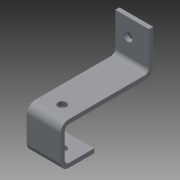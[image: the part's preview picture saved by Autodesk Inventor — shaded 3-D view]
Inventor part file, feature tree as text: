
AUTODESK INVENTOR PART (.ipt)
format: ipt  version: 2013 (Build 170138000, 138)  size: 134,144 bytes
history: native  units: in
note: dims shown in document units (in); Inventor stores cm internally (conversion verified against a paired STEP export)
features: sheet_metal_op x10, sketch x5, other x4, extrude x1, reference x1
ambient origin geometry x8: Origin, YZ Plane, XZ Plane, XY Plane, X Axis, Y Axis, Z Axis, Center Point
bodies: Solid1 (feature_tree)
feature tree (21):
  sheet_metal_op  "Face1"
  sheet_metal_op  "Flange1"
  sheet_metal_op  "Flange2"
  sheet_metal_op  "Flange3"
  extrude  "Extrusion1"  Depth=0.125in
  sketch  "Sketch1"  dims[d0=0.125in d1=0.125in]
  other  "Plate1"
  sketch  "Sketch2"  dims[d2=0.0625in]
  other  "Plate2"
  sheet_metal_op  "Bend1"
  sheet_metal_op  "Corner1"
  sketch  "Sketch3"  dims[d3=0.25in]
  other  "Plate3"
  sheet_metal_op  "Bend2"
  sheet_metal_op  "Corner2"
  sketch  "Sketch4"  dims[d4=0.125in]
  other  "Plate4"
  sheet_metal_op  "Bend3"
  sheet_metal_op  "Corner3"
  sketch  "Sketch5"  dims[d5=2.5in d6=90.0deg d7=0.125in d8=0.5in d9=0.125in d10=0.125in d11=0.125in d12=0.0625in d13=0.25in d14=0.125in d15=1.0in d16=90.0deg d17=0.125in d18=0.5in d19=0.125in d20=0.125in d21=0.125in d22=0.0625in d23=0.25in d24=0.125in d25=1.0in d26=90.0deg d27=0.125in d28=0.5in d29=0.125in d30=0.125in d31=2.1in d33=1.2784in d34=0.25in d35=1.5in d36=0.0in d37=1.0in d38=0.375in]
  reference  "Reference1"
